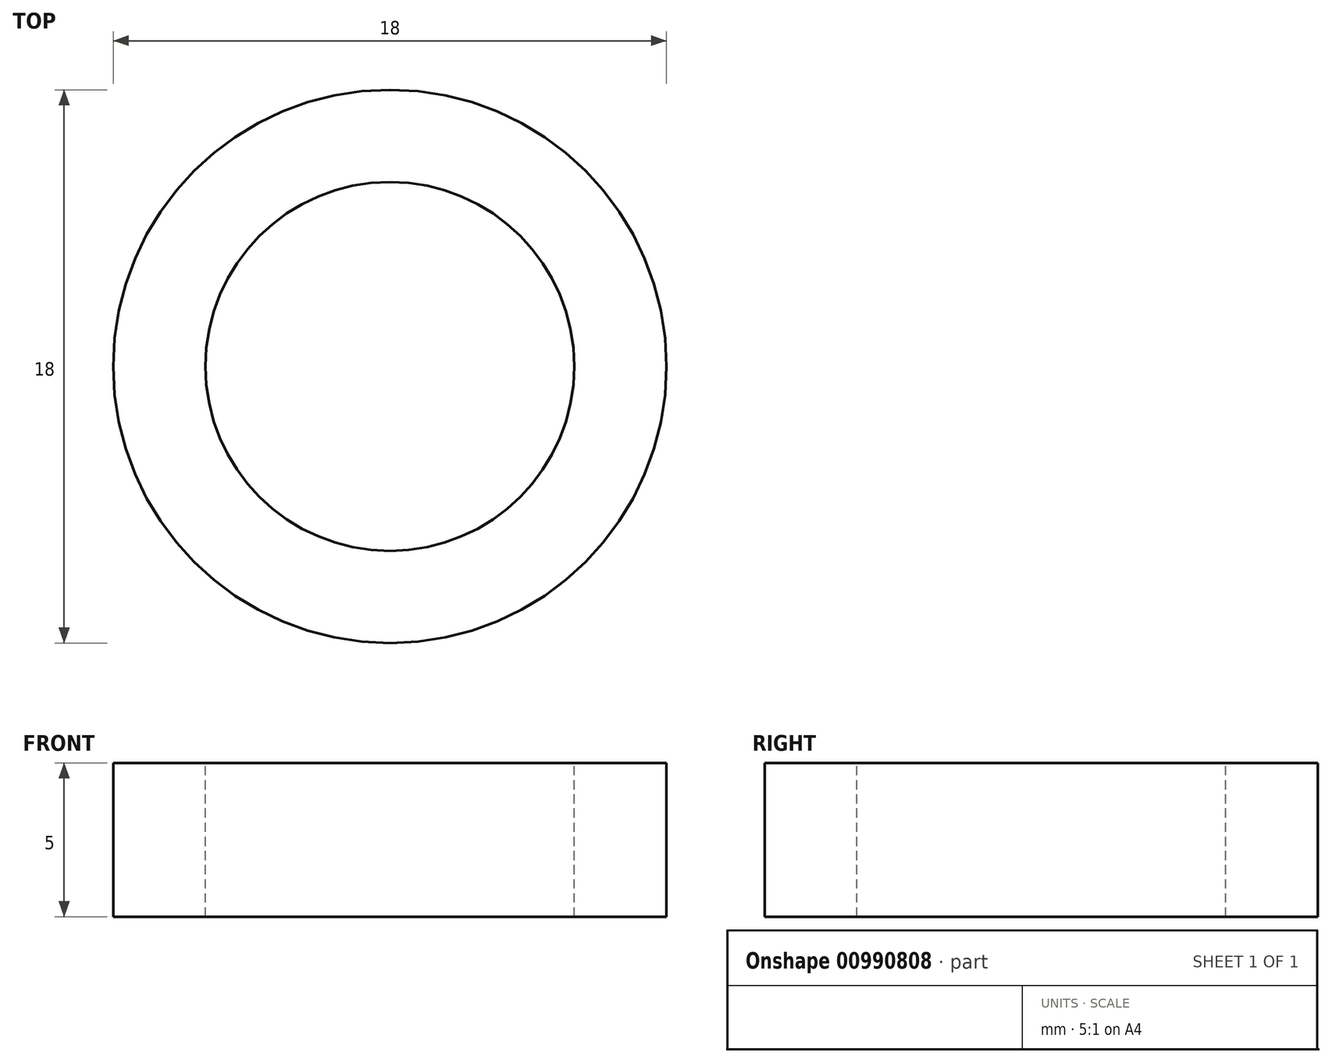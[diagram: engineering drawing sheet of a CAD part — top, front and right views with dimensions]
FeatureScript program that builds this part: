
annotation { "Feature Type Name" : "Feature", "Feature Type Description" : "" }
export const myFeature = defineFeature(function(context is Context, id is Id, definition is map)
    precondition{}
    {
        {
            var Q0;
            Q0=qCreatedBy(makeId("Top.planeOp"),FACE);
            var sketch = newSketch(context, id + "F0", { "sketchPlane" : qUnion([Q0])});
            skCircle(sketch, "E0", {"center": v(0, 0) * mm, "radius": 6 * mm});
            skSolve(sketch);
        }
        {
            var Q0;
            Q0=qCreatedBy(makeId("Top.planeOp"),FACE);
            var sketch = newSketch(context, id + "F1", { "sketchPlane" : qUnion([Q0])});
            skCircle(sketch, "E1.0", {"center": v(0, 0) * mm, "radius": 9 * mm});
            skSolve(sketch);
        }
        {
            var Q0;
            Q0=makeQuery(id+"F1.imprint","IMPRINT",FACE,{"disambiguationData":[TD([[makeQuery(id+"F1.imprint","IMPRINT",EDGE,{"derivedFrom":sQuery(id+"F1.wireOp",EDGE,"E1.0")}),1.0]])]});
            var Q1;
            Q1=sQuery(id+"F0.wireOp",EDGE,"E0");
            var Q2;
            Q2=sQuery(id+"F1.wireOp",EDGE,"E1.0");
            extrude(context, id + "F2", {"entities" : qUnion([Q0]), "surfaceEntities" : qUnion([Q1, Q2]), "depth" : 5 * mm, "offsetDistance" : 25 * mm});
        }
        {
            var Q0;
            Q0=makeQuery(id+"F2.opExtrude","CAP_FACE",FACE,{"disambiguationData":[OSD([sQuery(id+"F1.wireOp",EDGE,"E1.0")])],"isStart":false});
            var sketch = newSketch(context, id + "F3", { "sketchPlane" : qUnion([Q0])});
            skCircle(sketch, "E2", {"center": v(0, 0) * mm, "radius": 6 * mm});
            skSolve(sketch);
        }
        {
            var Q0;
            Q0 = qSketchRegion(id + "F3", true);
            extrude(context, id + "F4", {"entities" : qUnion([Q0]), "operationType" : NewBodyOperationType.REMOVE, "oppositeDirection" : true, "depth" : 25 * mm, "offsetDistance" : 25 * mm});
        }
    });
